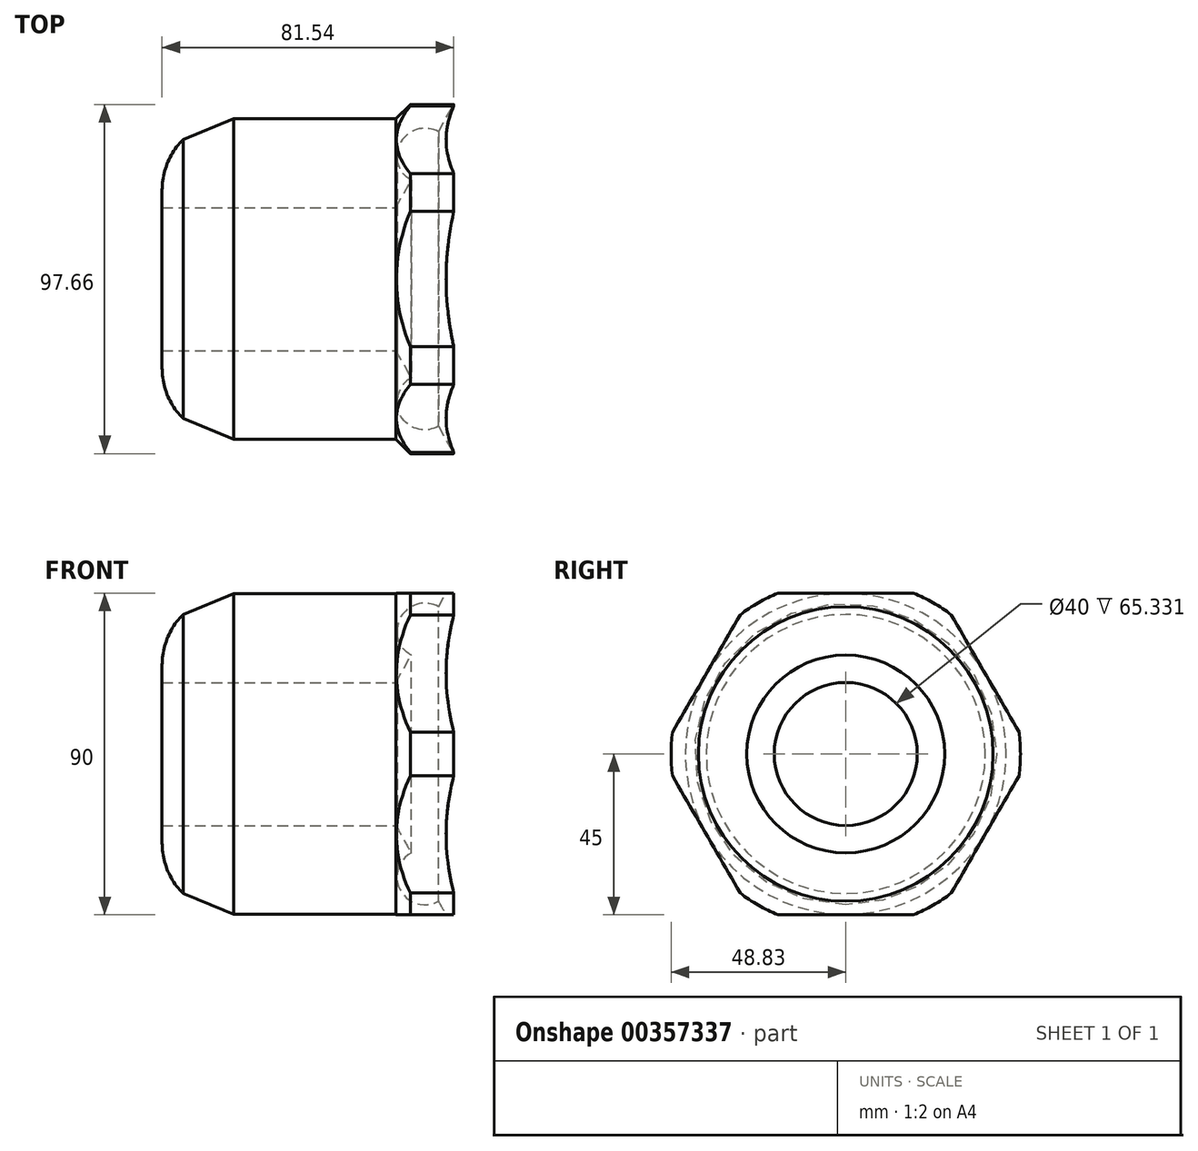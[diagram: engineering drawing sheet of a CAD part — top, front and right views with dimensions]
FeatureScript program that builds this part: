
annotation { "Feature Type Name" : "Feature", "Feature Type Description" : "" }
export const myFeature = defineFeature(function(context is Context, id is Id, definition is map)
    precondition{}
    {
        {
            var Q0;
            Q0=qCreatedBy(makeId("Front.planeOp"),FACE);
            var sketch = newSketch(context, id + "F0", { "sketchPlane" : qUnion([Q0])});
            skLineSegment(sketch, "E0.bottom", {"start": v(20, 20) * mm, "end": v(0, 20) * mm});
            skLineSegment(sketch, "E0.top", {"start": v(20, 0) * mm, "end": v(0, 0) * mm});
            skLineSegment(sketch, "E0.left", {"start": v(20, 20) * mm, "end": v(20, 0) * mm});
            skLineSegment(sketch, "E0.right", {"start": v(0, 20) * mm, "end": v(0, 0) * mm});
            skLineSegment(sketch, "E1.bottom", {"start": v(0, 20) * mm, "end": v(65.33, 20) * mm});
            skLineSegment(sketch, "E1.top", {"start": v(20, 44.86) * mm, "end": v(65.33, 44.86) * mm});
            skLineSegment(sketch, "E1.left", {"start": v(0, 20) * mm, "end": v(0, 24.86) * mm});
            skLineSegment(sketch, "E1.right", {"start": v(65.33, 20) * mm, "end": v(65.33, 44.86) * mm});
            skLineSegment(sketch, "E2", {"start": v(69.38, 48.83) * mm, "end": v(65.33, 44.86) * mm});
            skLineSegment(sketch, "E3", {"start": v(69.38, 48.83) * mm, "end": v(81.54, 48.83) * mm});
            skLineSegment(sketch, "E4", {"start": v(81.54, 48.83) * mm, "end": v(65.33, 20) * mm});
            skArc(sketch, "E5", {"start": v(77.24, 41.18) * mm, "mid": v(66.67, 38.22) * mm, "end": v(69.63, 27.65) * mm});
            skPoint(sketch, "E6.visualSharp", {"position": v(0, 44.86) * mm});
            skArc(sketch, "E6.filletArc", {"start": v(20, 44.86) * mm, "mid": v(5.86, 39) * mm, "end": v(0, 24.86) * mm});
            skLineSegment(sketch, "E7", {"start": v(20, 44.86) * mm, "end": v(5.86, 39) * mm});
            skSolve(sketch);
        }
        {
            var Q0;
            Q0=makeQuery(id+"F0.imprint","IMPRINT",FACE,{"disambiguationData":[TD([[makeQuery(id+"F0.imprint","IMPRINT",EDGE,{"derivedFrom":sQuery(id+"F0.wireOp",EDGE,"E1.top")}),-1.0]])]});
            var Q1;
            Q1=makeQuery(id+"F0.imprint","IMPRINT",FACE,{"disambiguationData":[TD([[makeQuery(id+"F0.imprint","IMPRINT",EDGE,{"derivedFrom":sQuery(id+"F0.wireOp",EDGE,"E1.right")}),-1.0]])]});
            var Q2;
            Q2=sQuery(id+"F0.wireOp",EDGE,"E0.top");
            revolve(context, id + "F1", {"entities" : qUnion([Q0, Q1]), "axis" : qUnion([Q2]), "revolveType" : RevolveType.FULL});
        }
        {
            var Q0;
            Q0=qCreatedBy(makeId("Right.planeOp"),FACE);
            var sketch = newSketch(context, id + "F2", { "sketchPlane" : qUnion([Q0])});
            skCircle(sketch, "E8.cCircle", {"center": v(0, 0) * mm, "radius": 45 * mm, "construction": true});
            skLineSegment(sketch, "E8.0", {"start": v(-25.98, 45) * mm, "end": v(25.98, 45) * mm});
            skLineSegment(sketch, "E8.1", {"start": v(25.98, 45) * mm, "end": v(51.96, 0) * mm});
            skLineSegment(sketch, "E8.2", {"start": v(51.96, 0) * mm, "end": v(25.98, -45) * mm});
            skLineSegment(sketch, "E8.3", {"start": v(25.98, -45) * mm, "end": v(-25.98, -45) * mm});
            skLineSegment(sketch, "E8.4", {"start": v(-25.98, -45) * mm, "end": v(-51.96, 0) * mm});
            skLineSegment(sketch, "E8.5", {"start": v(-51.96, 0) * mm, "end": v(-25.98, 45) * mm});
            skPoint(sketch, "E8.0.midPoint", {"position": v(0, 45) * mm});
            skCircle(sketch, "E9", {"center": v(0, 0) * mm, "radius": 117.13 * mm});
            skSolve(sketch);
        }
        {
            var Q0;
            Q0=makeQuery(id+"F2.imprint","IMPRINT",FACE,{"disambiguationData":[TD([[makeQuery(id+"F2.imprint","IMPRINT",EDGE,{"derivedFrom":sQuery(id+"F2.wireOp",EDGE,"E8.0")}),1.0]])]});
            extrude(context, id + "F3", {"entities" : qUnion([Q0]), "operationType" : NewBodyOperationType.REMOVE, "depth" : 157.9 * mm});
        }
    });
